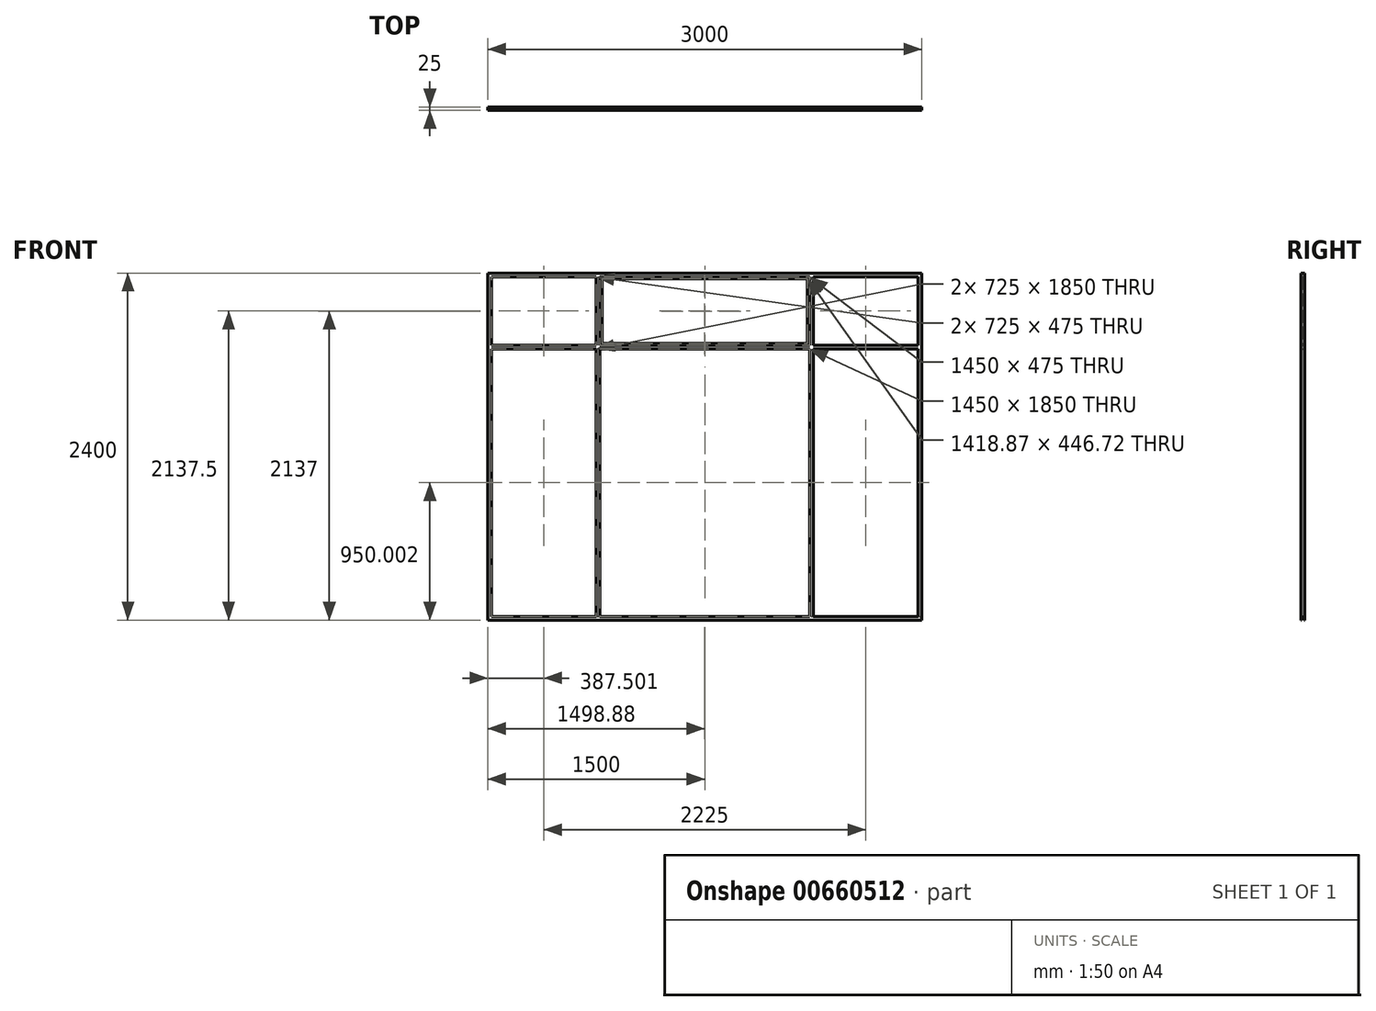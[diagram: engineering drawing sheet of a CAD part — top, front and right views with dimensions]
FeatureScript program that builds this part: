
annotation { "Feature Type Name" : "Feature", "Feature Type Description" : "" }
export const myFeature = defineFeature(function(context is Context, id is Id, definition is map)
    precondition{}
    {
        {
            var Q0;
            Q0=qCreatedBy(makeId("Front.planeOp"),FACE);
            var sketch = newSketch(context, id + "F0", { "sketchPlane" : qUnion([Q0])});
            skLineSegment(sketch, "E0.top", {"start": v(-1472.05, -1661.56) * mm, "end": v(1527.95, -1661.56) * mm});
            skLineSegment(sketch, "E0.right", {"start": v(1527.95, 738.44) * mm, "end": v(1527.95, -1661.56) * mm});
            skLineSegment(sketch, "E1", {"start": v(-1447.05, 238.44) * mm, "end": v(-722.05, 238.44) * mm});
            skLineSegment(sketch, "E2", {"start": v(-1472.05, 738.44) * mm, "end": v(-1472.05, 238.44) * mm});
            skLineSegment(sketch, "E3", {"start": v(-1472.05, 238.44) * mm, "end": v(-1472.05, -1661.56) * mm});
            skPoint(sketch, "E4", {"position": v(-697.05, 738.44) * mm});
            skLineSegment(sketch, "E5", {"start": v(-1472.05, 738.44) * mm, "end": v(-697.05, 738.44) * mm});
            skPoint(sketch, "E6", {"position": v(752.95, 738.44) * mm});
            skLineSegment(sketch, "E7", {"start": v(1527.95, 738.44) * mm, "end": v(752.95, 738.44) * mm});
            skLineSegment(sketch, "E8", {"start": v(-697.05, 738.44) * mm, "end": v(752.95, 738.44) * mm});
            skLineSegment(sketch, "E9", {"start": v(-697.05, 713.44) * mm, "end": v(-697.05, 238.44) * mm});
            skLineSegment(sketch, "E10", {"start": v(752.95, 713.44) * mm, "end": v(752.95, 238.44) * mm});
            skLineSegment(sketch, "E11.0", {"start": v(-1447.05, 713.44) * mm, "end": v(-1447.05, 238.44) * mm});
            skLineSegment(sketch, "E11.1", {"start": v(-1447.05, 213.44) * mm, "end": v(-1447.05, -1636.56) * mm});
            skLineSegment(sketch, "E11.2", {"start": v(-697.05, 713.44) * mm, "end": v(752.95, 713.44) * mm});
            skLineSegment(sketch, "E11.3", {"start": v(1502.95, 713.44) * mm, "end": v(777.95, 713.44) * mm});
            skLineSegment(sketch, "E11.4", {"start": v(1502.95, 713.44) * mm, "end": v(1502.95, 238.44) * mm});
            skLineSegment(sketch, "E11.5", {"start": v(-1447.05, 713.44) * mm, "end": v(-722.05, 713.44) * mm});
            skLineSegment(sketch, "E11.6", {"start": v(-1447.05, -1636.56) * mm, "end": v(-722.05, -1636.56) * mm});
            skLineSegment(sketch, "E12.0", {"start": v(-722.05, 713.44) * mm, "end": v(-722.05, 238.44) * mm});
            skLineSegment(sketch, "E13.0", {"start": v(777.95, 713.44) * mm, "end": v(777.95, 238.44) * mm});
            skLineSegment(sketch, "E14.0", {"start": v(-1447.05, 213.44) * mm, "end": v(-722.05, 213.44) * mm});
            skLineSegment(sketch, "E15.trimOffspring", {"start": v(-697.05, -1636.56) * mm, "end": v(752.95, -1636.56) * mm});
            skLineSegment(sketch, "E16.trimOffspring", {"start": v(777.95, -1636.56) * mm, "end": v(1502.95, -1636.56) * mm});
            skLineSegment(sketch, "E17.trimOffspring", {"start": v(1502.95, 213.44) * mm, "end": v(1502.95, -1636.56) * mm});
            skLineSegment(sketch, "E18.trimOffspring", {"start": v(752.95, 213.44) * mm, "end": v(752.95, -1636.56) * mm});
            skLineSegment(sketch, "E19.trimOffspring", {"start": v(777.95, 213.44) * mm, "end": v(777.95, -1636.56) * mm});
            skLineSegment(sketch, "E20.trimOffspring", {"start": v(-697.05, 238.44) * mm, "end": v(1502.95, 238.44) * mm});
            skLineSegment(sketch, "E21.trimOffspring", {"start": v(-697.05, 213.44) * mm, "end": v(-697.05, -1636.56) * mm});
            skLineSegment(sketch, "E22.trimOffspring", {"start": v(-722.05, 213.44) * mm, "end": v(-722.05, -1636.56) * mm});
            skLineSegment(sketch, "E23.trimOffspring", {"start": v(-697.05, 213.44) * mm, "end": v(1502.95, 213.44) * mm});
            skSolve(sketch);
        }
        {
            var Q0;
            Q0 = qSketchRegion(id + "F0", true);
            extrude(context, id + "F1", {"entities" : qUnion([Q0]), "endBound" : BoundingType.SYMMETRIC, "depth" : 25 * mm, "offsetDistance" : 25 * mm});
        }
        {
            var Q0;
            Q0 = qSketchRegion(id + "F0", true);
            extrude(context, id + "F2", {"entities" : qUnion([Q0]), "operationType" : NewBodyOperationType.ADD, "endBound" : BoundingType.SYMMETRIC, "depth" : 25 * mm, "offsetDistance" : 25 * mm});
        }
        {
            var Q0;
            Q0=makeQuery(id+"F1.opExtrude","SWEPT_FACE",FACE,{"disambiguationData":[OSD([sQuery(id+"F0.wireOp",EDGE,"E2"),sQuery(id+"F0.wireOp",EDGE,"E3")])]});
            var sketch = newSketch(context, id + "F3", { "sketchPlane" : qUnion([Q0])});
            skLineSegment(sketch, "E24.bottom", {"start": v(-9.5, -1661.56) * mm, "end": v(9.5, -1661.56) * mm});
            skLineSegment(sketch, "E24.top", {"start": v(-9.5, -1641.56) * mm, "end": v(9.5, -1641.56) * mm});
            skLineSegment(sketch, "E24.left", {"start": v(-9.5, -1661.56) * mm, "end": v(-9.5, -1641.56) * mm});
            skLineSegment(sketch, "E24.right", {"start": v(9.5, -1661.56) * mm, "end": v(9.5, -1641.56) * mm});
            skSolve(sketch);
        }
        {
            var Q0;
            Q0=makeQuery(id+"F3.imprint","IMPRINT",FACE,{"disambiguationData":[TD([[makeQuery(id+"F3.imprint","IMPRINT",EDGE,{"derivedFrom":sQuery(id+"F3.wireOp",EDGE,"E24.bottom")}),-1.0]])]});
            var Q1;
            Q1=makeQuery(id+"F1.opExtrude","SWEPT_FACE",FACE,{"disambiguationData":[OSD([sQuery(id+"F0.wireOp",EDGE,"E0.right")])]});
            extrude(context, id + "F4", {"entities" : qUnion([Q0]), "operationType" : NewBodyOperationType.REMOVE, "endBound" : BoundingType.UP_TO_SURFACE, "oppositeDirection" : true, "depth" : 25 * mm, "endBoundEntityFace" : qUnion([Q1]), "offsetDistance" : 25 * mm});
        }
        {
            var Q0;
            Q0=qCreatedBy(makeId("Front.planeOp"),FACE);
            var sketch = newSketch(context, id + "F5", { "sketchPlane" : qUnion([Q0])});
            skLineSegment(sketch, "E25.bottom", {"start": v(-702.6, 718.8) * mm, "end": v(756.26, 718.8) * mm});
            skLineSegment(sketch, "E25.top", {"start": v(-702.6, 232.09) * mm, "end": v(756.26, 232.09) * mm});
            skLineSegment(sketch, "E25.left", {"start": v(-702.6, 718.8) * mm, "end": v(-702.6, 232.09) * mm});
            skLineSegment(sketch, "E25.right", {"start": v(756.26, 718.8) * mm, "end": v(756.26, 232.09) * mm});
            skLineSegment(sketch, "E26.0", {"start": v(-697.6, 721.24) * mm, "end": v(-697.6, 232.09) * mm});
            skLineSegment(sketch, "E27.0", {"start": v(-682.6, 698.8) * mm, "end": v(736.26, 698.8) * mm});
            skLineSegment(sketch, "E27.1", {"start": v(-682.6, 698.8) * mm, "end": v(-682.6, 252.09) * mm});
            skLineSegment(sketch, "E27.2", {"start": v(-682.6, 252.09) * mm, "end": v(736.26, 252.09) * mm});
            skLineSegment(sketch, "E27.3", {"start": v(736.26, 698.8) * mm, "end": v(736.26, 252.09) * mm});
            skSolve(sketch);
        }
        {
            var Q0;
            Q0 = qSketchRegion(id + "F5", true);
            extrude(context, id + "F6", {"entities" : qUnion([Q0]), "operationType" : NewBodyOperationType.ADD, "endBound" : BoundingType.SYMMETRIC, "depth" : 3 * mm, "offsetDistance" : 25 * mm});
        }
    });
